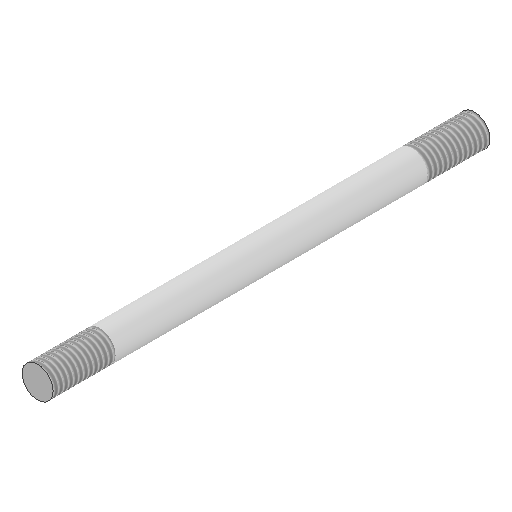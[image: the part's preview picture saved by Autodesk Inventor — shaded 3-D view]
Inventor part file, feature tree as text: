
AUTODESK INVENTOR PART (.ipt)
format: ipt  version: 2025.1 (Build 291241000, 241)  size: 98,816 bytes
history: native  units: mm
features: thread x2, other x1, extrude x1, sketch x1
ambient origin geometry x8: Origin, YZ Plane, XZ Plane, XY Plane, X Axis, Y Axis, Z Axis, Center Point
bodies: Body1 (feature_tree)
feature tree (5):
  other  "Bryła1"
  extrude  "Wyciągnięcie proste1"  Depth=5.0mm
  thread  "Gwint1"
  thread  "Gwint2"
  sketch  "Szkic1"
